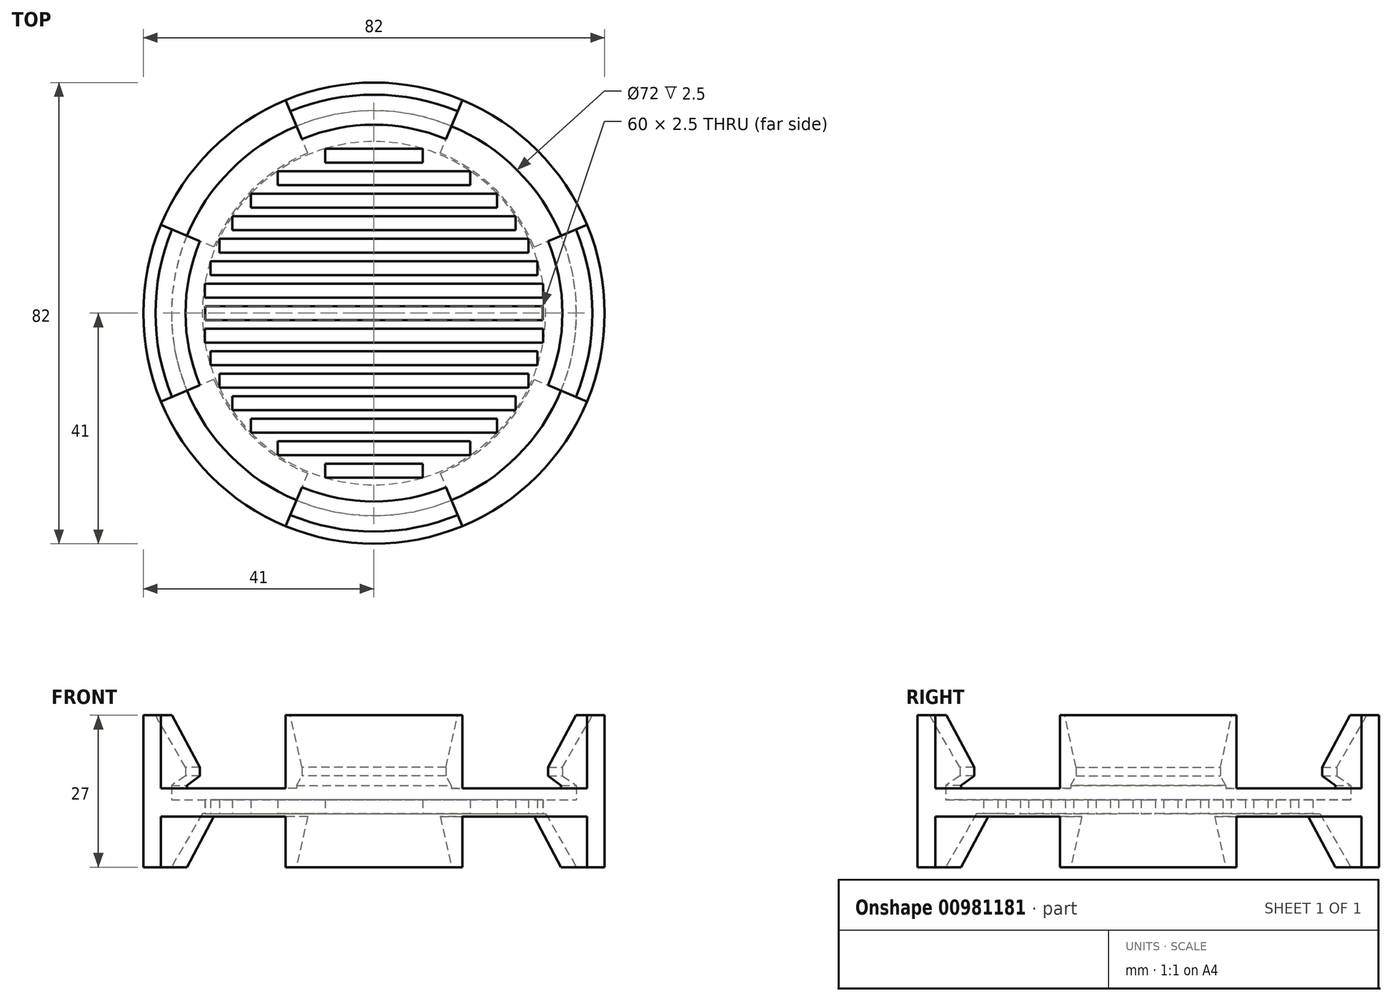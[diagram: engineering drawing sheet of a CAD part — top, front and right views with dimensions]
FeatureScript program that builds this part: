
annotation { "Feature Type Name" : "Feature", "Feature Type Description" : "" }
export const myFeature = defineFeature(function(context is Context, id is Id, definition is map)
    precondition{}
    {
        {
            var Q0;
            Q0=qCreatedBy(makeId("Front.planeOp"),FACE);
            var sketch = newSketch(context, id + "F0", { "sketchPlane" : qUnion([Q0])});
            skLineSegment(sketch, "E0", {"start": v(0, 9.5) * mm, "end": v(0, 64.55) * mm, "construction": true});
            skLineSegment(sketch, "E1", {"start": v(-36, 0) * mm, "end": v(-41, 0) * mm});
            skLineSegment(sketch, "E2", {"start": v(-41, 0) * mm, "end": v(-41, 27) * mm});
            skLineSegment(sketch, "E3", {"start": v(-41, 27) * mm, "end": v(-38.84, 27) * mm});
            skLineSegment(sketch, "E4", {"start": v(-38.84, 27) * mm, "end": v(-33.5, 17.75) * mm});
            skLineSegment(sketch, "E5", {"start": v(-33.5, 17.75) * mm, "end": v(-33.5, 16.25) * mm});
            skLineSegment(sketch, "E6", {"start": v(-33.5, 16.25) * mm, "end": v(-36, 14.5) * mm});
            skLineSegment(sketch, "E7", {"start": v(-36, 14.5) * mm, "end": v(-36, 12) * mm});
            skLineSegment(sketch, "E8", {"start": v(-36, 12) * mm, "end": v(0, 12) * mm});
            skLineSegment(sketch, "E9", {"start": v(0, 12) * mm, "end": v(0, 9.5) * mm});
            skPoint(sketch, "E10", {"position": v(-33.5, 17) * mm});
            skLineSegment(sketch, "E11", {"start": v(-36, 0) * mm, "end": v(-30.52, 9.5) * mm});
            skLineSegment(sketch, "E12", {"start": v(-30.52, 9.5) * mm, "end": v(0, 9.5) * mm});
            skPoint(sketch, "E13.orphan", {"position": v(0, 0) * mm});
            skSolve(sketch);
        }
        {
            var Q0;
            Q0 = qSketchRegion(id + "F0", true);
            var Q1;
            Q1=sQuery(id+"F0.wireOp",EDGE,"E0");
            revolve(context, id + "F1", {"surfaceOperationType" : NewSurfaceOperationType.NEW, "entities" : qUnion([Q0]), "axis" : qUnion([Q1]), "revolveType" : RevolveType.FULL});
        }
        {
            var Q0;
            Q0=makeQuery(id+"F1.opRevolve","SWEPT_FACE",FACE,{"disambiguationData":[OSD([sQuery(id+"F0.wireOp",EDGE,"E1")])]});
            var sketch = newSketch(context, id + "F2", { "sketchPlane" : qUnion([Q0])});
            skLineSegment(sketch, "E14", {"start": v(0, 0) * mm, "end": v(37.88, 15.7) * mm});
            skLineSegment(sketch, "E15", {"start": v(0, 0) * mm, "end": v(15.7, 37.88) * mm});
            skArc(sketch, "E16", {"start": v(15.7, 37.88) * mm, "mid": v(29, 29) * mm, "end": v(37.88, 15.7) * mm});
            skLineSegment(sketch, "E17.1.0", {"start": v(0, 0) * mm, "end": v(-15.7, 37.88) * mm});
            skLineSegment(sketch, "E17.1.1", {"start": v(0, 0) * mm, "end": v(-37.88, 15.7) * mm});
            skArc(sketch, "E17.1.2", {"start": v(-37.88, 15.7) * mm, "mid": v(-29, 29) * mm, "end": v(-15.7, 37.88) * mm});
            skLineSegment(sketch, "E17.2.0", {"start": v(0, 0) * mm, "end": v(-37.88, -15.7) * mm});
            skLineSegment(sketch, "E17.2.1", {"start": v(0, 0) * mm, "end": v(-15.7, -37.88) * mm});
            skArc(sketch, "E17.2.2", {"start": v(-15.7, -37.88) * mm, "mid": v(-29, -29) * mm, "end": v(-37.88, -15.7) * mm});
            skLineSegment(sketch, "E17.3.0", {"start": v(0, 0) * mm, "end": v(15.7, -37.88) * mm});
            skLineSegment(sketch, "E17.3.1", {"start": v(0, 0) * mm, "end": v(37.88, -15.7) * mm});
            skArc(sketch, "E17.3.2", {"start": v(37.88, -15.7) * mm, "mid": v(29, -29) * mm, "end": v(15.7, -37.88) * mm});
            skSolve(sketch);
        }
        {
            var Q0;
            Q0 = qSketchRegion(id + "F2", true);
            extrude(context, id + "F3", {"entities" : qUnion([Q0]), "operationType" : NewBodyOperationType.REMOVE, "oppositeDirection" : true, "depth" : 9 * mm, "offsetDistance" : 25 * mm});
        }
        {
            var Q0;
            Q0=makeQuery(id+"F1.opRevolve","SWEPT_FACE",FACE,{"disambiguationData":[OSD([sQuery(id+"F0.wireOp",EDGE,"E12")])]});
            var sketch = newSketch(context, id + "F4", { "sketchPlane" : qUnion([Q0])});
            skLineSegment(sketch, "E18", {"start": v(0, 30.52) * mm, "end": v(0, -30.52) * mm, "construction": true});
            skLineSegment(sketch, "E19.bottom", {"start": v(30, -1.25) * mm, "end": v(-30, -1.25) * mm});
            skLineSegment(sketch, "E19.top", {"start": v(30, 1.25) * mm, "end": v(-30, 1.25) * mm});
            skLineSegment(sketch, "E19.left", {"start": v(30, -1.25) * mm, "end": v(30, 1.25) * mm});
            skLineSegment(sketch, "E19.right", {"start": v(-30, -1.25) * mm, "end": v(-30, 1.25) * mm});
            skPoint(sketch, "E19.middle", {"position": v(0, 0) * mm});
            skLineSegment(sketch, "E20.bottom", {"start": v(30.06, -5.25) * mm, "end": v(-30.06, -5.25) * mm});
            skLineSegment(sketch, "E20.top", {"start": v(30.06, -2.75) * mm, "end": v(-30.06, -2.75) * mm});
            skLineSegment(sketch, "E20.left", {"start": v(30.06, -5.25) * mm, "end": v(30.06, -2.75) * mm});
            skLineSegment(sketch, "E20.right", {"start": v(-30.06, -5.25) * mm, "end": v(-30.06, -2.75) * mm});
            skPoint(sketch, "E20.middle", {"position": v(0, -4) * mm});
            skLineSegment(sketch, "E21.bottom", {"start": v(29.08, -9.25) * mm, "end": v(-29.08, -9.25) * mm});
            skLineSegment(sketch, "E21.top", {"start": v(29.08, -6.75) * mm, "end": v(-29.08, -6.75) * mm});
            skLineSegment(sketch, "E21.left", {"start": v(29.08, -9.25) * mm, "end": v(29.08, -6.75) * mm});
            skLineSegment(sketch, "E21.right", {"start": v(-29.08, -9.25) * mm, "end": v(-29.08, -6.75) * mm});
            skPoint(sketch, "E21.middle", {"position": v(0, -8) * mm});
            skLineSegment(sketch, "E22.bottom", {"start": v(27.49, -13.25) * mm, "end": v(-27.49, -13.25) * mm});
            skLineSegment(sketch, "E22.top", {"start": v(27.49, -10.75) * mm, "end": v(-27.49, -10.75) * mm});
            skLineSegment(sketch, "E22.left", {"start": v(27.49, -13.25) * mm, "end": v(27.49, -10.75) * mm});
            skLineSegment(sketch, "E22.right", {"start": v(-27.49, -13.25) * mm, "end": v(-27.49, -10.75) * mm});
            skPoint(sketch, "E22.middle", {"position": v(0, -12) * mm});
            skLineSegment(sketch, "E23.bottom", {"start": v(25.17, -17.25) * mm, "end": v(-25.17, -17.25) * mm});
            skLineSegment(sketch, "E23.top", {"start": v(25.17, -14.75) * mm, "end": v(-25.17, -14.75) * mm});
            skLineSegment(sketch, "E23.left", {"start": v(25.17, -17.25) * mm, "end": v(25.17, -14.75) * mm});
            skLineSegment(sketch, "E23.right", {"start": v(-25.17, -17.25) * mm, "end": v(-25.17, -14.75) * mm});
            skPoint(sketch, "E23.middle", {"position": v(0, -16) * mm});
            skLineSegment(sketch, "E24.bottom", {"start": v(21.9, -21.25) * mm, "end": v(-21.9, -21.25) * mm});
            skLineSegment(sketch, "E24.top", {"start": v(21.9, -18.75) * mm, "end": v(-21.9, -18.75) * mm});
            skLineSegment(sketch, "E24.left", {"start": v(21.9, -21.25) * mm, "end": v(21.9, -18.75) * mm});
            skLineSegment(sketch, "E24.right", {"start": v(-21.9, -21.25) * mm, "end": v(-21.9, -18.75) * mm});
            skPoint(sketch, "E24.middle", {"position": v(0, -20) * mm});
            skLineSegment(sketch, "E25.bottom", {"start": v(8.7, -29.25) * mm, "end": v(-8.7, -29.25) * mm});
            skLineSegment(sketch, "E25.top", {"start": v(8.7, -26.75) * mm, "end": v(-8.7, -26.75) * mm});
            skLineSegment(sketch, "E25.left", {"start": v(8.7, -29.25) * mm, "end": v(8.7, -26.75) * mm});
            skLineSegment(sketch, "E25.right", {"start": v(-8.7, -29.25) * mm, "end": v(-8.7, -26.75) * mm});
            skPoint(sketch, "E25.middle", {"position": v(0, -28) * mm});
            skLineSegment(sketch, "E26.bottom", {"start": v(-17.14, -22.75) * mm, "end": v(17.14, -22.75) * mm});
            skLineSegment(sketch, "E26.top", {"start": v(-17.14, -25.25) * mm, "end": v(17.14, -25.25) * mm});
            skLineSegment(sketch, "E26.left", {"start": v(-17.14, -22.75) * mm, "end": v(-17.14, -25.25) * mm});
            skLineSegment(sketch, "E26.right", {"start": v(17.14, -22.75) * mm, "end": v(17.14, -25.25) * mm});
            skPoint(sketch, "E26.middle", {"position": v(0, -24) * mm});
            skLineSegment(sketch, "E27", {"start": v(0, 0) * mm, "end": v(-23.84, 0) * mm, "construction": true});
            skLineSegment(sketch, "E28.MirrorCS", {"start": v(-17.14, 22.75) * mm, "end": v(-17.14, 25.25) * mm});
            skLineSegment(sketch, "E29.MirrorCS", {"start": v(-30.06, 5.25) * mm, "end": v(-30.06, 2.75) * mm});
            skLineSegment(sketch, "E30.MirrorCS", {"start": v(25.17, 14.75) * mm, "end": v(-25.17, 14.75) * mm});
            skLineSegment(sketch, "E31.MirrorCS", {"start": v(27.49, 13.25) * mm, "end": v(-27.49, 13.25) * mm});
            skPoint(sketch, "E32.MirrorP", {"position": v(0, 24) * mm});
            skLineSegment(sketch, "E33.MirrorCS", {"start": v(8.7, 29.25) * mm, "end": v(8.7, 26.75) * mm});
            skPoint(sketch, "E34.MirrorP", {"position": v(0, 28) * mm});
            skLineSegment(sketch, "E35.MirrorCS", {"start": v(21.9, 21.25) * mm, "end": v(21.9, 18.75) * mm});
            skLineSegment(sketch, "E36.MirrorCS", {"start": v(-21.9, 21.25) * mm, "end": v(-21.9, 18.75) * mm});
            skPoint(sketch, "E37.MirrorP", {"position": v(0, 16) * mm});
            skLineSegment(sketch, "E38.MirrorCS", {"start": v(29.08, 9.25) * mm, "end": v(29.08, 6.75) * mm});
            skLineSegment(sketch, "E39.MirrorCS", {"start": v(8.7, 29.25) * mm, "end": v(-8.7, 29.25) * mm});
            skLineSegment(sketch, "E40.MirrorCS", {"start": v(8.7, 26.75) * mm, "end": v(-8.7, 26.75) * mm});
            skPoint(sketch, "E41.MirrorP", {"position": v(0, 12) * mm});
            skLineSegment(sketch, "E42.MirrorCS", {"start": v(29.08, 6.75) * mm, "end": v(-29.08, 6.75) * mm});
            skLineSegment(sketch, "E43.MirrorCS", {"start": v(-17.14, 22.75) * mm, "end": v(17.14, 22.75) * mm});
            skLineSegment(sketch, "E44.MirrorCS", {"start": v(30.06, 2.75) * mm, "end": v(-30.06, 2.75) * mm});
            skLineSegment(sketch, "E45.MirrorCS", {"start": v(-25.17, 17.25) * mm, "end": v(-25.17, 14.75) * mm});
            skPoint(sketch, "E46.MirrorP", {"position": v(0, 8) * mm});
            skLineSegment(sketch, "E47.MirrorCS", {"start": v(-8.7, 29.25) * mm, "end": v(-8.7, 26.75) * mm});
            skLineSegment(sketch, "E48.MirrorCS", {"start": v(25.17, 17.25) * mm, "end": v(25.17, 14.75) * mm});
            skPoint(sketch, "E49.MirrorP", {"position": v(0, 4) * mm});
            skLineSegment(sketch, "E50.MirrorCS", {"start": v(-29.08, 9.25) * mm, "end": v(-29.08, 6.75) * mm});
            skLineSegment(sketch, "E51.MirrorCS", {"start": v(-27.49, 13.25) * mm, "end": v(-27.49, 10.75) * mm});
            skLineSegment(sketch, "E52.MirrorCS", {"start": v(21.9, 21.25) * mm, "end": v(-21.9, 21.25) * mm});
            skLineSegment(sketch, "E53.MirrorCS", {"start": v(27.49, 13.25) * mm, "end": v(27.49, 10.75) * mm});
            skLineSegment(sketch, "E54.MirrorCS", {"start": v(21.9, 18.75) * mm, "end": v(-21.9, 18.75) * mm});
            skLineSegment(sketch, "E55.MirrorCS", {"start": v(29.08, 9.25) * mm, "end": v(-29.08, 9.25) * mm});
            skLineSegment(sketch, "E56.MirrorCS", {"start": v(-17.14, 25.25) * mm, "end": v(17.14, 25.25) * mm});
            skLineSegment(sketch, "E57.MirrorCS", {"start": v(30.06, 5.25) * mm, "end": v(30.06, 2.75) * mm});
            skLineSegment(sketch, "E58.MirrorCS", {"start": v(25.17, 17.25) * mm, "end": v(-25.17, 17.25) * mm});
            skPoint(sketch, "E59.MirrorP", {"position": v(0, 20) * mm});
            skLineSegment(sketch, "E60.MirrorCS", {"start": v(27.49, 10.75) * mm, "end": v(-27.49, 10.75) * mm});
            skLineSegment(sketch, "E61.MirrorCS", {"start": v(17.14, 22.75) * mm, "end": v(17.14, 25.25) * mm});
            skLineSegment(sketch, "E62.MirrorCS", {"start": v(30.06, 5.25) * mm, "end": v(-30.06, 5.25) * mm});
            skSolve(sketch);
        }
        {
            var Q0;
            Q0 = qSketchRegion(id + "F4", true);
            extrude(context, id + "F5", {"entities" : qUnion([Q0]), "operationType" : NewBodyOperationType.REMOVE, "endBound" : BoundingType.UP_TO_NEXT, "oppositeDirection" : true, "depth" : 10 * mm, "offsetDistance" : 25 * mm, "hasSecondDirection" : true, "secondDirectionOppositeDirection" : false, "secondDirectionDepth" : 25 * mm});
        }
        {
            var Q0;
            Q0=makeQuery(id+"F1.opRevolve","SWEPT_FACE",FACE,{"disambiguationData":[OSD([sQuery(id+"F0.wireOp",EDGE,"E3")])]});
            var sketch = newSketch(context, id + "F6", { "sketchPlane" : qUnion([Q0])});
            skLineSegment(sketch, "E63", {"start": v(0, 0) * mm, "end": v(-15.7, -37.88) * mm});
            skLineSegment(sketch, "E64", {"start": v(0, 0) * mm, "end": v(-37.88, -15.7) * mm});
            skArc(sketch, "E65", {"start": v(-15.7, -37.88) * mm, "mid": v(-29, -29) * mm, "end": v(-37.88, -15.7) * mm});
            skLineSegment(sketch, "E66.1.0", {"start": v(0, 0) * mm, "end": v(37.88, -15.7) * mm});
            skLineSegment(sketch, "E66.1.1", {"start": v(0, 0) * mm, "end": v(15.7, -37.88) * mm});
            skArc(sketch, "E66.1.2", {"start": v(37.88, -15.7) * mm, "mid": v(29, -29) * mm, "end": v(15.7, -37.88) * mm});
            skLineSegment(sketch, "E66.2.0", {"start": v(0, 0) * mm, "end": v(15.7, 37.88) * mm});
            skLineSegment(sketch, "E66.2.1", {"start": v(0, 0) * mm, "end": v(37.88, 15.7) * mm});
            skArc(sketch, "E66.2.2", {"start": v(15.7, 37.88) * mm, "mid": v(29, 29) * mm, "end": v(37.88, 15.7) * mm});
            skLineSegment(sketch, "E66.3.0", {"start": v(0, 0) * mm, "end": v(-37.88, 15.7) * mm});
            skLineSegment(sketch, "E66.3.1", {"start": v(0, 0) * mm, "end": v(-15.7, 37.88) * mm});
            skArc(sketch, "E66.3.2", {"start": v(-37.88, 15.7) * mm, "mid": v(-29, 29) * mm, "end": v(-15.7, 37.88) * mm});
            skSolve(sketch);
        }
        {
            var Q0;
            Q0 = qSketchRegion(id + "F6", true);
            extrude(context, id + "F7", {"entities" : qUnion([Q0]), "operationType" : NewBodyOperationType.REMOVE, "oppositeDirection" : true, "depth" : 13 * mm, "offsetDistance" : 25 * mm});
        }
    });
